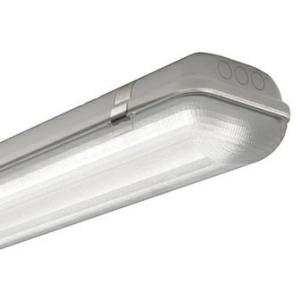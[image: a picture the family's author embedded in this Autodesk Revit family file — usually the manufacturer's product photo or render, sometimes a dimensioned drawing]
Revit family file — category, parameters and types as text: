
# Revit family: 3f_filippi_-_3f_linda_3f_filippi_-_58619_-_3f_linda_led_2x22w_l1570
name_source: partatom
category: Lighting Fixtures
units: mm (PartAtom-declared; Revit-internal decimal feet)

## family parameters
Cut with Voids When Loaded = No
Host = Face
Light Source = No
Part Type = Normal
Room Calculation Point = No
Round Connector Dimension = Use Diameter
Shared = No

## types (1)
- 3F Filippi - 3F Linda (1 x LED, 7557 lm, 49 W, 4000 K)
    Apparent Load = 49 VA
    Approval mark = CE
    CIE Flux Codes = 46 76 93 97 100
    Color Rendering = 80
    Color Temperature = 4000 K
    Control Gear = Electronic ballast
    Default Elevation = 1800 mm
    Description = ILLUMINOTECHNICAL
Luminous efficiency 100% (DLOR 97%, ULOR 3%).
Initial luminous flux of the luminaire 7557 lm.
Controlled symmetric distribution.
Installation Interdistance Transv.D = 1.52 x hu - Long.D = 1.17 x hu.
Tabular UGR (CIE 117 - 4H-8H; S=0.25H; 70/50/20): RUG 23.5 - 22.7.
Beam angle: 94° - 78°.
Luminous efficacy 154 lm/W.
Lifetime (L93/B10): 30000 h. (tq+25°C)
Lifetime (L90/B10): 50000 h. (tq+25°C)
Lifetime (L85/B10): 80000 h. (tq+25°C)
Lifetime (L80/B10): 100000 h. (tq+25°C)
Lifetime (L85/B10): 50000 h. (tq+40°C)
Sudden decreased luminous flux after 50000 hours: 0% (C0).
Photobiological safety in compliance with IEC/TR 62778: RG0 risk exempt, (IEC 62471).
In compliance with IEC/EN 62722-2-1 - IEC/EN 62717 standards.

SOURCE
2 linear LED modules 22W/840.
Energy efficiency class (UE 2019/2020 - UE 2019/2015): D.
CIE 13.3 Colour rendering index: CRI >80 (R9 <50%).
IES TM-30 Fidelity Index: Rf = 84 Rg = 95.
CCT nominal colour temperature 4000 K.
Colour initial tolerance (MacAdam): SDCM 3.

MECHANICAL
Self-extinguishing V2 polycarbonate housing, injection moulded, RAL 7035 grey.
Ecologic anti-aging injected sealing gasket.
Diffuser in self-extinguishing V2 polycarbonate, photo-engraved interior, UV stabilised, injection moulded with smooth outer surface, tamper-proof opening.
Gear-holder reflector in hot-dip galvanised steel, painted with white polyester base.
Snug fit safety snap-lock clips for diffuser mounting in stainless steel, screwdriver opening.
Fixing brackets in stainless steel.
Possibility for technicians to access the interior of the luminaire.
Luminaire with limited surface temperature. - D - (EN 60598-2-24)
Dimensions: 1570x160 mm, height 100 mm. Weight 3.2 kg.
IP66 protection degree.
Mechanical strength to impacts IK10 (20 joule).
Glow-wire test resistance 850°C.

ELECTRICAL
Halogen Free electronic wiring 230V-50/60Hz, power factor 0.97, THD <25%, constant output current, SELV, class I, 1 driver.
Power of the luminaire 49 W.
ENEC - CE.
SAFE FLICKER: PstLM=<1 and SVM=<0.4 (IEC TR 61547-1 and IEC TR 63158), to ensure a more comfortable and safe light.
Luminaire compliant with EN 60598-2-22 for power supply from a centralised emergency system CPSS (Central Power Supply System), not incorporated in the luminaire - high risk areas excluded. The default power and flux are 100% in AC and 100% in DC.
Ambient temperature from -20°C to +40°C.
Temperature class T6 max 85°C.
Relative humidity UR: <85%.

INSTALLATION
Ceiling / Suspended / Wall.
All accessories dedicated to this product are available on the Catalog and on our website www.3F-Filippi.com.

APPLICATIONS
Suitable product for food production plants (HACCP), IFS (Food Version 6), BRC (GSFS Food Version 7).
Dry, dusty indoor environments, subject to occasional water splashes.
Virtually shatterproof polycarbonate compatibly with the fumes / atmospheres that compromise the elasticity of plastic materials.
Not suitable for installation on surfaces subject to important vibrations, exposed to weather conditions, on ropes or poles.
Suitable for illumination of public car parks and parking grounds referred to DIN 67528:2018-04.

WARNING
Fixture not suitable for cold stores with an ambient temperature <0°C and/or relative humidity >85%.
Luminaire designed for disposal/recycling at end-of-life.
Replaceable (LED only) light source by a professional. Replaceable control gear by a professional.
    Height = 100 mm  [stored 0.328084 ft]
    Lamp = 1 x LED
    Lamp Light Flux = 7557 lm
    Lamp Power = 49 W
    Lamp count = 1
    Length = 1570 mm
    Lifetime = 50000 h
    Luminous efficacy = 154 lm/W
    Manufacturer = 3F Filippi
    ModVariant = No
    Model = 3F Filippi - 58619 - 3F Linda LED 2x22W L1570
    Mounting Place = Ceiling
    Mounting Type = Pendant
    Number of Poles = 1
    OnlyDefault = Yes
    Power Factor = 1
    Product Name = 3F Filippi - 3F Linda
    Product group = pendant luminaire
    ProductGroupID = 9
    Protection Class = Protection class I
    Protection Degree = IP 66
    RLX_Detail_Level = 1
    RLX_Emergency_Light_Flux = 0 lm
    RLX_Emergency_Type = 0
    RLX_Emergency_Type_DB = No
    RlxData = <blob elided: 71549 chars, md5=c2bad27f>
    Socket = socket
    Standby Power = 0 W
    System Light Flux = 7557 lm
    System Power = 49 W
    Type Comments = Product without accessories
    Type Image = 3ffilippi_3f_linda_led_2x.jpg
    URL = http://relux.com
    VarID = ---
    Voltage = 0 V
    Weight = 0.00 kg
    Width = 160 mm

note: [stored X ft] marks values corroborated as IEEE doubles in the binary element streams (Revit-internal decimal feet)

## geometry (parser evidence)
native form markers: Blend x4, Sweep x10
no freeform markers — native parametric forms only
